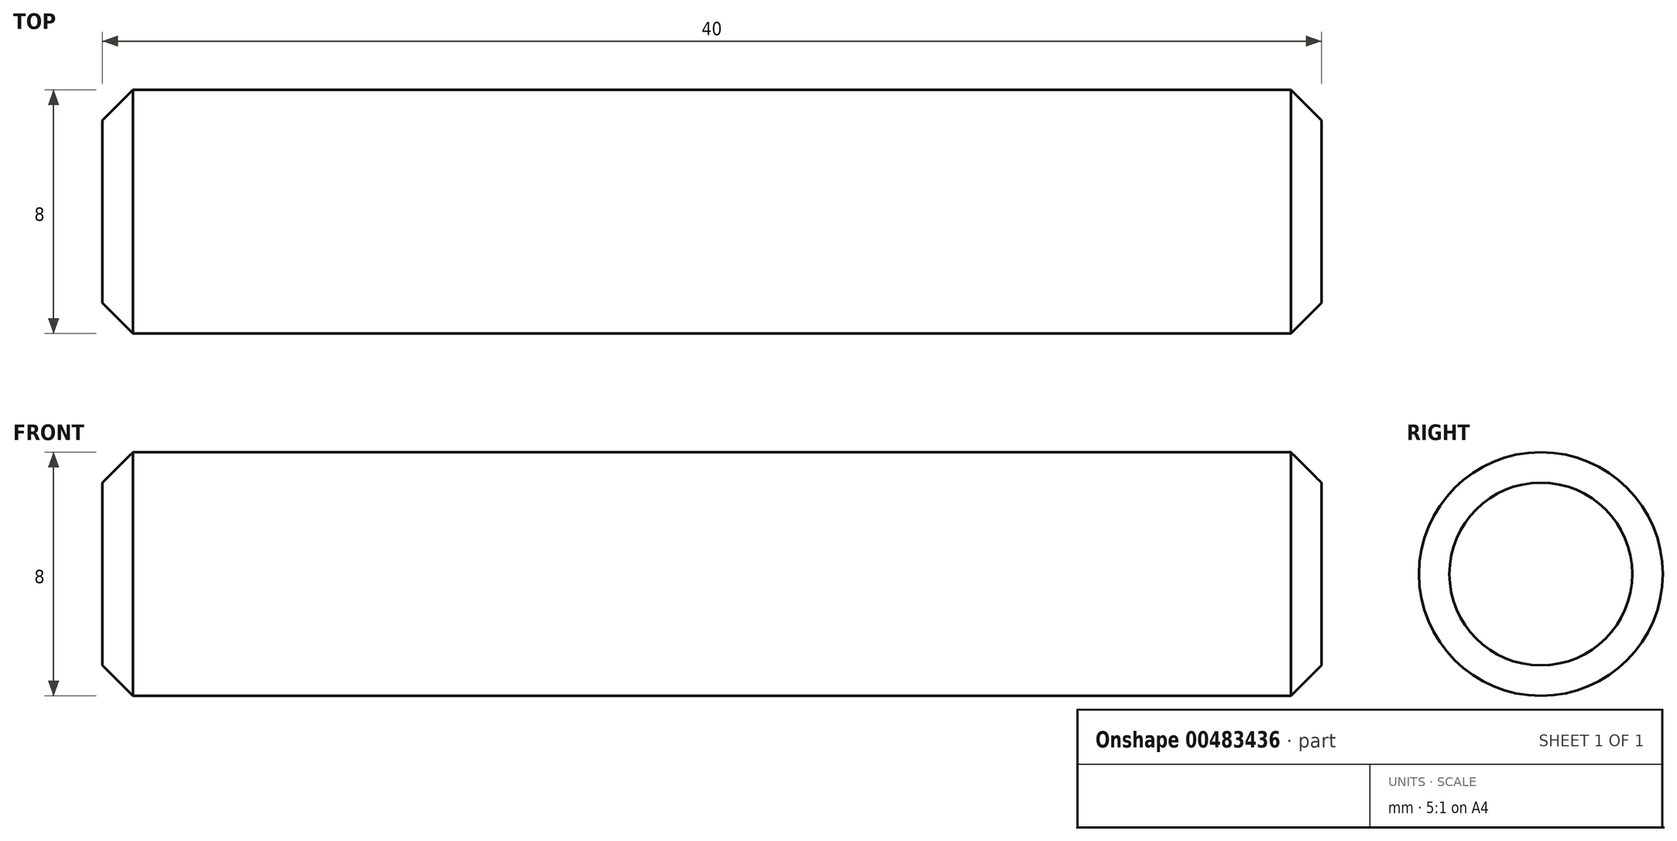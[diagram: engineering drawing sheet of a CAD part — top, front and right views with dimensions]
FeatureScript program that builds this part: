
annotation { "Feature Type Name" : "Feature", "Feature Type Description" : "" }
export const myFeature = defineFeature(function(context is Context, id is Id, definition is map)
    precondition{}
    {
        {
            var Q0;
            Q0=qCreatedBy(makeId("Front.planeOp"),FACE);
            var sketch = newSketch(context, id + "F0", { "sketchPlane" : qUnion([Q0])});
            skLineSegment(sketch, "E0.bottom", {"start": v(-20, 0) * mm, "end": v(20, 0) * mm});
            skLineSegment(sketch, "E0.top", {"start": v(-20, -4) * mm, "end": v(20, -4) * mm});
            skLineSegment(sketch, "E0.left", {"start": v(-20, 0) * mm, "end": v(-20, -4) * mm});
            skLineSegment(sketch, "E0.right", {"start": v(20, 0) * mm, "end": v(20, -4) * mm});
            skSolve(sketch);
        }
        {
            var Q0;
            Q0=makeQuery(id+"F0.imprint","IMPRINT",FACE,{"disambiguationData":[TD([[makeQuery(id+"F0.imprint","IMPRINT",EDGE,{"derivedFrom":sQuery(id+"F0.wireOp",EDGE,"E0.bottom")}),-1.0]])]});
            var Q1;
            Q1=sQuery(id+"F0.wireOp",EDGE,"E0.bottom");
            revolve(context, id + "F1", {"entities" : qUnion([Q0]), "axis" : qUnion([Q1]), "revolveType" : RevolveType.FULL});
        }
        {
            var Q0;
            Q0=makeQuery(id+"F1.opRevolve","SWEPT_EDGE",EDGE,{"disambiguationData":[OSD([sQuery(id+"F0.wireOp",EDGE,"E0.top"),sQuery(id+"F0.wireOp",EDGE,"E0.left")])]});
            var Q1;
            Q1=makeQuery(id+"F1.opRevolve","SWEPT_EDGE",EDGE,{"disambiguationData":[OSD([sQuery(id+"F0.wireOp",EDGE,"E0.top"),sQuery(id+"F0.wireOp",EDGE,"E0.right")])]});
            chamfer(context, id + "F2", {"entities" : qUnion([Q0, Q1]), "width" : 1 * mm, "tangentPropagation" : true});
        }
    });
